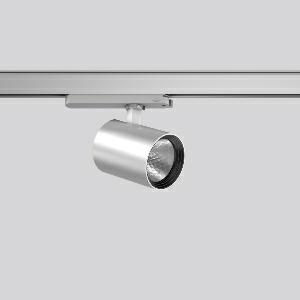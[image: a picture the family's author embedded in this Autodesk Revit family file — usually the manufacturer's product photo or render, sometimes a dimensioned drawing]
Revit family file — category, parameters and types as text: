
# Revit family: deecos_s_mini_track-in_742252_004_9326
name_source: partatom
category: Lighting Fixtures
units: mm (PartAtom-declared; Revit-internal decimal feet)

## family parameters
Cut with Voids When Loaded = No
Host = Face
Light Source = No
Part Type = Normal
Room Calculation Point = No
Round Connector Dimension = Use Diameter
Shared = No

## types (1)
- DEECOS S mini track-in (1 x LED Modul 930, 2550 lm, 3000)
    Apparent Load = 20 VA
    Approval mark = CE
    CIE Flux Codes = 95 99 100 100 100
    Color Rendering = 90
    Color Temperature = 3000
    Default Elevation = 1800 mm
    Description = Series: DEECOS S mini track-in
LED surface-mounted projector in modern design with no visible cooling ribs. Housing: die-cast aluminium, powder-coated. Rotation range: 356°. Swivel range: 90°. Black plastic ring and recessed LED to prevent glare from the side. Optical assembly with reflector made of MIRO-Silver with 98% total light reflection for outstanding efficiency - can be changed without tools. Best colour rendering index Ra>90. With multi adaptor for 3-circuit tracks 230 V. Suitable for Track on ceiling, Wall track. Track-in driver integrated into the adapter. High quality converter without flickering and stroboscopic effect. The following accessories can be mounted without use of tools: interchangeable lenses, decorative glasses, honeycomb louvre, clear and frosted diffusers, white interchangeable plastic ring. 
Colour: silver
Diameter: 87 mm
Height: 135 mm
Lamp: LED
Socket: without socket
Colour temperature: 3000K
Colour rendering index (CRI): 92
System power: 20 W
Rated luminous flux: 2550 lm
Luminous efficiency: 128 lm/W
Control gear: Regulated power supply
Protection class: II
Type of protection: IP 20
    Height = 135 mm
    Lamp = 1 x LED Modul 930
    Lamp Light Flux = 2550 lm
    Lamp count = 1
    Length = 87 mm
    Lifetime = 50000 h
    Luminous efficacy = 128 lm/W
    Manufacturer = RZB
    ModVariant = No
    Model = 742252.004
    Mounting Place = Ceiling
    Mounting Type = Rail mounted
    Number of Poles = 1
    OnlyDefault = Yes
    Power Factor = 1
    Product Name = DEECOS S mini track-in
    Product group = Track mounted projectors
    ProductGroupID = 301
    Protection Class = Protection class II
    Protection Degree = IP 20
    RLX_Detail_Level = 1
    RLX_Emergency_Light_Flux = 0 lm
    RLX_Emergency_Type = 0
    RLX_Emergency_Type_DB = No
    RlxData = <blob elided: 36249 chars, md5=5e041ca1>
    Socket = socket
    Standby Power = 0 W
    System Light Flux = 2550 lm
    System Power = 20 W
    Type Comments = Product without accessories
    Type Image = 742098.004.jpg
    URL = http://relux.com
    VarID = ---
    Voltage = 230 V
    Voltage Range = 220-240 V
    Weight = 0.00 kg
    Width = 0 mm  [stored 0 ft]

note: [stored X ft] marks values corroborated as IEEE doubles in the binary element streams (Revit-internal decimal feet)

## geometry (parser evidence)
native form markers: Blend x4, Sweep x11
no freeform markers — native parametric forms only
